# Revit family: Table-Teknion-CQTDK_Single_Desk-R2020
name_source: partatom
category: Furniture
units: mm (PartAtom-declared; Revit-internal decimal feet)

## family parameters
Always vertical = Yes
Cut with Voids When Loaded = No
OmniClass Number = 23.40.20.00
OmniClass Title = General Furniture and Specialties
Room Calculation Point = No
Shared = Yes
Work Plane-Based = No

## types (4) — shared parameters
Assembly Code = E2020200
Manufacturer = Teknion
Manufacturer Fax = 416.661.4586
Part Number = CQTDK
Product Documentation Link = https://assets.teknion.com
Product Line = Desks
Product Page URL = https://www.teknion.com
Series = Routes
Sustainability Data = https://www.teknion.com
URL = www.teknion.com
Unit Weight URL = http://www.teknion.com
Warranty = http://www.teknion.com
zero-valued in all types: Default Elevation

## per-type parameters (varying)
| type | Caster | Description | Fixed Legs | Legs W60 | Legs W72 | Model | Width |
| Mobile 60 | Yes | Single Desk, Mobile Configuration, 30"Dx60"W | No | Yes | No | CQTDKM3060 | 60 " |
| Mobile 72 | Yes | Single Desk, Mobile Configuration, 30Dx72W | No | No | Yes | CQTDKM3072 | 72 " |
| Fixed 60 | No | Single Desk, Fixed Configuration, 30"Dx60"W | Yes | Yes | No | CQTDKF3060 | 60 " |
| Fixed 72 | No | Single Desk, Fixed Configuration, 30"Dx72"W | Yes | No | Yes | CQTDKF3072 | 72 " |

## geometry (parser evidence)
native form markers: Sweep x4
no freeform markers — native parametric forms only
